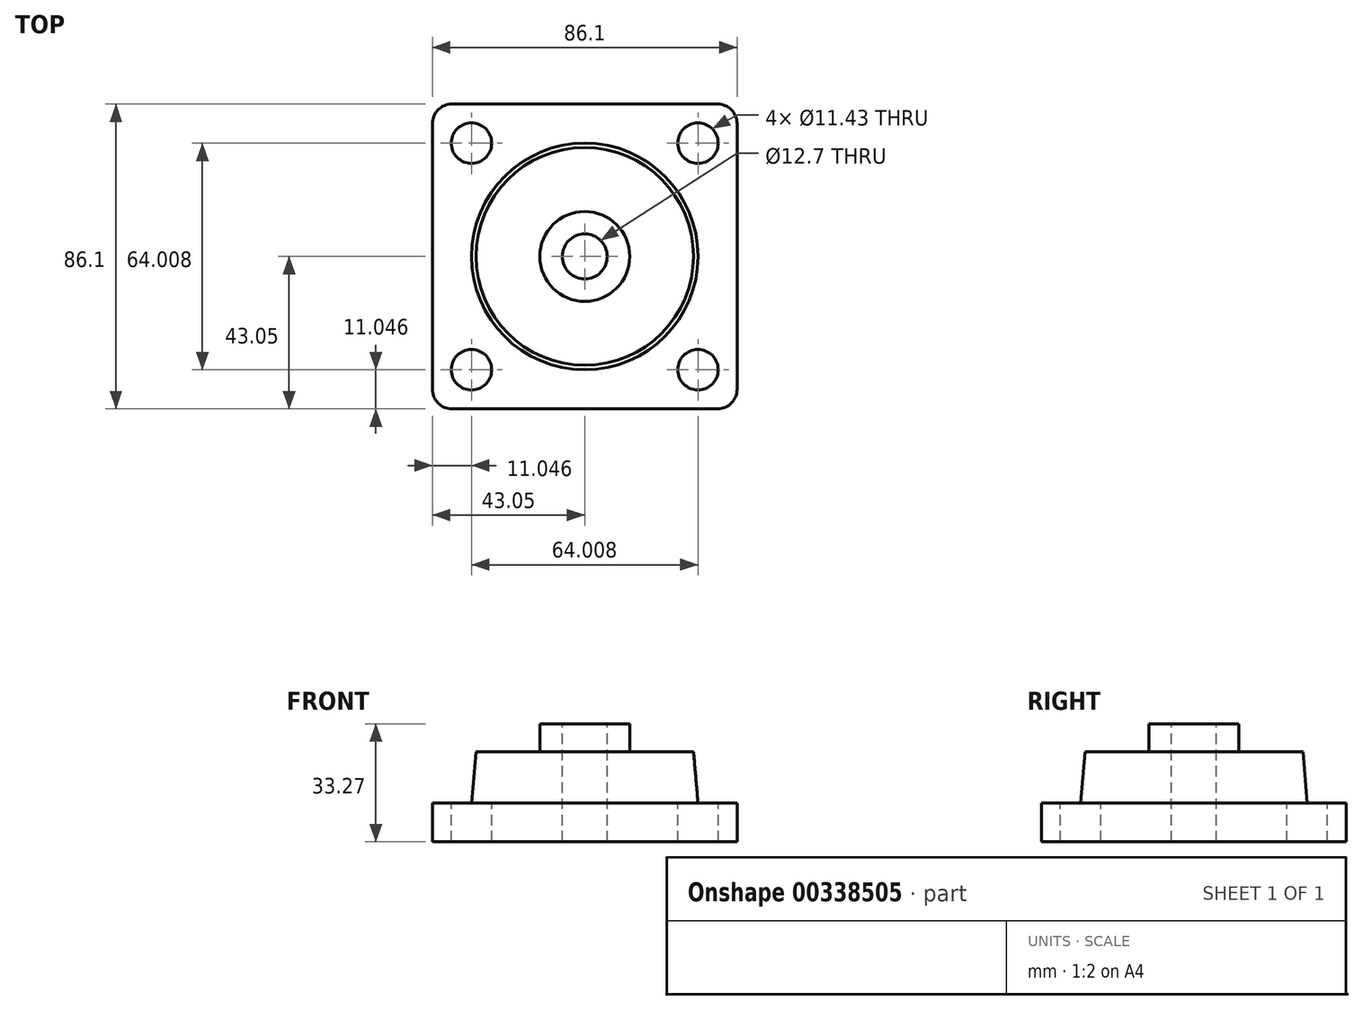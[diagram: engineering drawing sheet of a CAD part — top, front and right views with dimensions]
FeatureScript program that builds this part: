
annotation { "Feature Type Name" : "Feature", "Feature Type Description" : "" }
export const myFeature = defineFeature(function(context is Context, id is Id, definition is map)
    precondition{}
    {
        {
            var Q0;
            Q0=qCreatedBy(makeId("Top.planeOp"),FACE);
            var sketch = newSketch(context, id + "F0", { "sketchPlane" : qUnion([Q0])});
            skLineSegment(sketch, "E0.bottom", {"start": v(-43.05, 43.05) * mm, "end": v(43.05, 43.05) * mm});
            skLineSegment(sketch, "E0.top", {"start": v(-43.05, -43.05) * mm, "end": v(43.05, -43.05) * mm});
            skLineSegment(sketch, "E0.left", {"start": v(-43.05, 43.05) * mm, "end": v(-43.05, -43.05) * mm});
            skLineSegment(sketch, "E0.right", {"start": v(43.05, 43.05) * mm, "end": v(43.05, -43.05) * mm});
            skPoint(sketch, "E1", {"position": v(0, 43.05) * mm});
            skPoint(sketch, "E2", {"position": v(-43.05, 0) * mm});
            skSolve(sketch);
        }
        {
            var Q0;
            Q0=makeQuery(id+"F0.imprint","IMPRINT",FACE,{"disambiguationData":[TD([[makeQuery(id+"F0.imprint","IMPRINT",EDGE,{"derivedFrom":sQuery(id+"F0.wireOp",EDGE,"E0.bottom")}),-1.0]])]});
            extrude(context, id + "F1", {"entities" : qUnion([Q0]), "depth" : 10.92 * mm});
        }
        {
            var Q0;
            Q0=makeQuery(id+"F1.opExtrude","CAP_FACE",FACE,{"disambiguationData":[OSD([sQuery(id+"F0.wireOp",EDGE,"E0.bottom"),sQuery(id+"F0.wireOp",EDGE,"E0.top"),sQuery(id+"F0.wireOp",EDGE,"E0.left"),sQuery(id+"F0.wireOp",EDGE,"E0.right")])],"isStart":false});
            var sketch = newSketch(context, id + "F2", { "sketchPlane" : qUnion([Q0])});
            skPoint(sketch, "E3", {"position": v(-32, 32) * mm});
            skPoint(sketch, "E4", {"position": v(-32, -32) * mm});
            skPoint(sketch, "E5", {"position": v(32, -32) * mm});
            skPoint(sketch, "E6", {"position": v(32, 32) * mm});
            skSolve(sketch);
        }
        {
            var Q0;
            Q0=sQuery(id+"F2.wireOp",VERTEX,"E3");
            var Q1;
            Q1=sQuery(id+"F2.wireOp",VERTEX,"E6");
            var Q2;
            Q2=sQuery(id+"F2.wireOp",VERTEX,"E5");
            var Q3;
            Q3=sQuery(id+"F2.wireOp",VERTEX,"E4");
            var Q4;
            Q4=makeQuery(id+"F1.opExtrude","SWEPT_BODY",BODY,{"disambiguationData":[OSD([sQuery(id+"F0.wireOp",EDGE,"E0.bottom"),sQuery(id+"F0.wireOp",EDGE,"E0.top"),sQuery(id+"F0.wireOp",EDGE,"E0.left"),sQuery(id+"F0.wireOp",EDGE,"E0.right")])]});
            hole(context, id + "F3", {"style" : HoleStyle.SIMPLE, "endStyle" : HoleEndStyle.THROUGH, "holeDiameter" : 11.43 * mm, "isTappedThrough" : true, "tappedDepth" : 12.7 * mm, "tapClearance" : 3, "startFromSketch" : true, "locations" : qUnion([Q0, Q1, Q2, Q3]), "scope" : qUnion([Q4])});
        }
        {
            var Q0;
            Q0=makeQuery(id+"F1.opExtrude","CAP_FACE",FACE,{"disambiguationData":[OSD([sQuery(id+"F0.wireOp",EDGE,"E0.bottom"),sQuery(id+"F0.wireOp",EDGE,"E0.top"),sQuery(id+"F0.wireOp",EDGE,"E0.left"),sQuery(id+"F0.wireOp",EDGE,"E0.right")])],"isStart":false});
            var sketch = newSketch(context, id + "F4", { "sketchPlane" : qUnion([Q0])});
            skLineSegment(sketch, "E7", {"start": v(-32, 32) * mm, "end": v(32, 32) * mm});
            skCircle(sketch, "E8", {"center": v(0, 0) * mm, "radius": 32 * mm});
            skSolve(sketch);
        }
        {
            var Q0;
            Q0=makeQuery(id+"F4.imprint","IMPRINT",FACE,{"disambiguationData":[TD([[makeQuery(id+"F4.imprint","IMPRINT",EDGE,{"derivedFrom":sQuery(id+"F4.wireOp",EDGE,"E8")}),1.0]])]});
            extrude(context, id + "F5", {"entities" : qUnion([Q0]), "operationType" : NewBodyOperationType.ADD, "depth" : 14.48 * mm, "hasDraft" : true, "draftAngle" : 5 * degree, "draftPullDirection" : true});
        }
        {
            var Q0;
            Q0=makeQuery(id+"F5.opExtrude","CAP_FACE",FACE,{"disambiguationData":[OSD([sQuery(id+"F4.wireOp",EDGE,"E8")])],"isStart":false});
            var sketch = newSketch(context, id + "F6", { "sketchPlane" : qUnion([Q0])});
            skCircle(sketch, "E9", {"center": v(0, 0) * mm, "radius": 12.7 * mm});
            skSolve(sketch);
        }
        {
            var Q0;
            Q0=makeQuery(id+"F6.imprint","IMPRINT",FACE,{"disambiguationData":[TD([[makeQuery(id+"F6.imprint","IMPRINT",EDGE,{"derivedFrom":sQuery(id+"F6.wireOp",EDGE,"E9")}),1.0]])]});
            extrude(context, id + "F7", {"entities" : qUnion([Q0]), "operationType" : NewBodyOperationType.ADD, "depth" : 7.87 * mm});
        }
        {
            var Q0;
            Q0=makeQuery(id+"F7.opExtrude","CAP_FACE",FACE,{"disambiguationData":[OSD([sQuery(id+"F6.wireOp",EDGE,"E9")])],"isStart":false});
            var sketch = newSketch(context, id + "F8", { "sketchPlane" : qUnion([Q0])});
            skPoint(sketch, "E10", {"position": v(0, 0) * mm});
            skSolve(sketch);
        }
        {
            var Q0;
            Q0=sQuery(id+"F8.wireOp",VERTEX,"E10");
            var Q1;
            Q1=makeQuery(id+"F1.opExtrude","SWEPT_BODY",BODY,{"disambiguationData":[OSD([sQuery(id+"F0.wireOp",EDGE,"E0.bottom"),sQuery(id+"F0.wireOp",EDGE,"E0.top"),sQuery(id+"F0.wireOp",EDGE,"E0.left"),sQuery(id+"F0.wireOp",EDGE,"E0.right")])]});
            hole(context, id + "F9", {"style" : HoleStyle.SIMPLE, "endStyle" : HoleEndStyle.THROUGH, "holeDiameter" : 12.7 * mm, "isTappedThrough" : true, "tappedDepth" : 12.7 * mm, "tapClearance" : 3, "startFromSketch" : true, "locations" : qUnion([Q0]), "scope" : qUnion([Q1])});
        }
        {
            var Q0;
            Q0=makeQuery(id+"F1.opExtrude","SWEPT_EDGE",EDGE,{"disambiguationData":[OSD([sQuery(id+"F0.wireOp",EDGE,"E0.bottom"),sQuery(id+"F0.wireOp",EDGE,"E0.right")])]});
            var Q1;
            Q1=makeQuery(id+"F1.opExtrude","SWEPT_EDGE",EDGE,{"disambiguationData":[OSD([sQuery(id+"F0.wireOp",EDGE,"E0.top"),sQuery(id+"F0.wireOp",EDGE,"E0.right")])]});
            var Q2;
            Q2=makeQuery(id+"F1.opExtrude","SWEPT_EDGE",EDGE,{"disambiguationData":[OSD([sQuery(id+"F0.wireOp",EDGE,"E0.top"),sQuery(id+"F0.wireOp",EDGE,"E0.left")])]});
            var Q3;
            Q3=makeQuery(id+"F1.opExtrude","SWEPT_EDGE",EDGE,{"disambiguationData":[OSD([sQuery(id+"F0.wireOp",EDGE,"E0.bottom"),sQuery(id+"F0.wireOp",EDGE,"E0.left")])]});
            fillet(context, id + "F10", {"entities" : qUnion([Q0, Q1, Q2, Q3]), "radius" : 5.52 * mm, "tangentPropagation" : true, "allowEdgeOverflow" : false});
        }
    });
